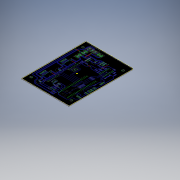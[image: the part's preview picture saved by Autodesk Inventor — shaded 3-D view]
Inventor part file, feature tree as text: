
AUTODESK INVENTOR PART (.ipt)
format: ipt  version: 2019 (Build 230136000, 136)  size: 168,448 bytes
history: native  units: mm
features: sketch x2, extrude x1, other x1
ambient origin geometry x8: Origin, YZ Plane, XZ Plane, XY Plane, X Axis, Y Axis, Z Axis, Center Point
bodies: Solid1 (feature_tree)
feature tree (4):
  extrude  "Extrusion1"  Depth=90.0mm
  sketch  "Sketch2"  dims[d2=82.0mm d3=110.0mm d4=3.2mm d5=3.2mm d6=3.2mm d7=3.2mm d8=1.0mm d9=0.0mm]
  sketch  "Sketch1"  dims[d0=70.0mm d1=90.0mm]
  other  "Image1"
